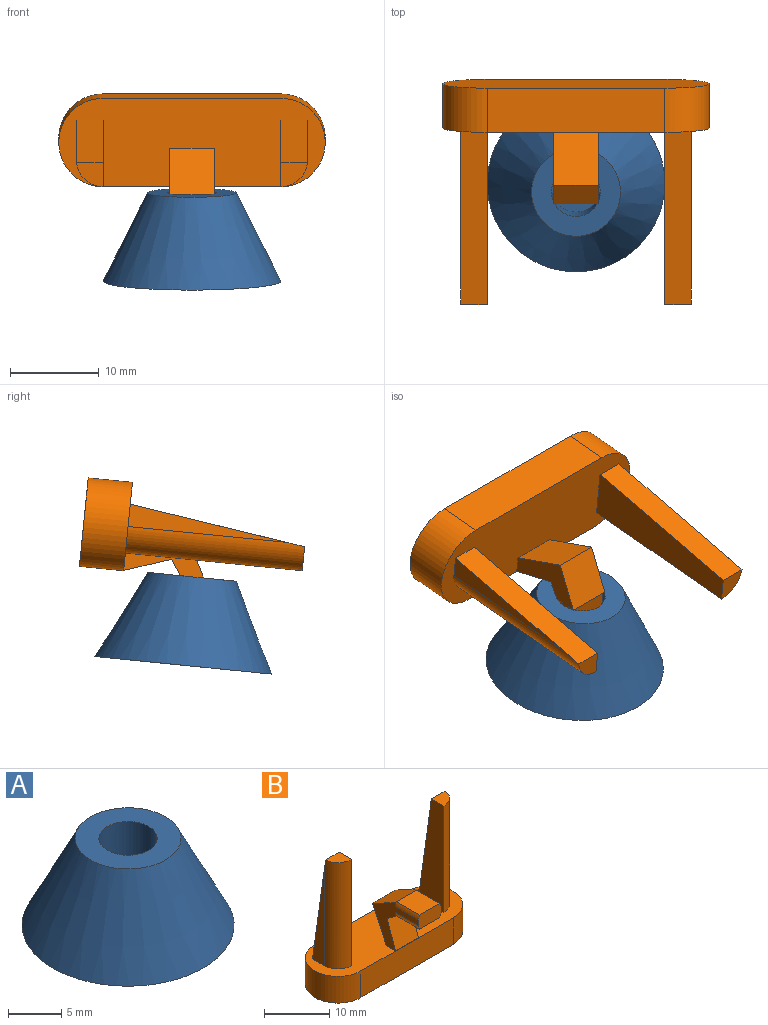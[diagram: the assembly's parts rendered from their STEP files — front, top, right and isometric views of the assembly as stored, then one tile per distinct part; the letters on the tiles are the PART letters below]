
ASSEMBLY  parts=2 mates=1
PART A: 5 faces, bbox 20x20x10 mm
  f0: plane 10x10mm, normal (0,0,1), area 54.8mm2, adj f2,f3
  f1: plane 20x20mm, normal (0,0,-1), area 314.2mm2, adj f2
  f2: cone r=5mm half-angle=26.6deg, axis (0,0,-1), area 526.9mm2, adj f0,f1
  f3: cylinder r=2.75mm len=5.5mm, axis (0,0,1), area 86.4mm2, adj f0,f4
  f4: plane 5.5x5.5mm, normal (0,0,1), area 23.8mm2, adj f3
PART B: 33 faces, bbox 30x14.9x25 mm
  f0: plane 0.82x0.32mm, normal (0,-1,0), area 0.1mm2, adj f22,f25,f31
  f1: plane 0.82x0.32mm, normal (0,-1,0), area 0.1mm2, adj f20,f25,f30
  f2: plane 0.82x0.32mm, normal (0,-1,0), area 0.1mm2, adj f20,f24,f28
  f3: plane 30x10mm, normal (0,0,1), area 239.4mm2, adj f4,f5,f6,f7,f9,f10,f11,f12
  f4: plane 20x5mm, normal (0,1,0), area 100mm2, adj f3,f5,f7,f8
  f5: cylinder r=5mm len=10mm, axis (0,0,-1), area 78.5mm2, adj f3,f4,f6,f8
  f6: plane 20x5mm, normal (0,-1,0), area 100mm2, adj f3,f5,f7,f8
  f7: cylinder r=5mm len=10mm, axis (0,0,-1), area 78.5mm2, adj f3,f4,f6,f8
  f8: plane 30x10mm, normal (0,0,-1), area 278.5mm2, adj f4,f5,f6,f7
  f9: plane 17.95x2.52mm, normal (-1,0,0), area 22.7mm2, adj f3,f10,f12
  f10: cylinder r=3mm len=20mm, axis (0,0,-1), area 94mm2, adj f3,f9,f11,f12,f13
  f11: plane 20x5.52mm, normal (1,0,0), area 82.4mm2, adj f3,f10,f12,f13
  f12: plane 20x3mm, normal (0,0.99,0.14), area 60.6mm2, adj f3,f9,f10,f11,f13
  f13: plane 2.99x2.71mm, normal (0,0,1), area 6.2mm2, adj f10,f11,f12
  f14: plane 20x3mm, normal (0,0.99,0.14), area 60.6mm2, adj f3,f15,f16,f17,f18
  f15: plane 20x5.52mm, normal (-1,0,0), area 82.4mm2, adj f3,f14,f16,f18
  f16: cylinder r=3mm len=20mm, axis (0,0,-1), area 94mm2, adj f3,f14,f15,f17,f18
  f17: plane 17.95x2.52mm, normal (1,0,0), area 22.7mm2, adj f3,f14,f16
  f18: plane 2.99x2.71mm, normal (0,0,1), area 6.2mm2, adj f14,f15,f16
  f19: plane 6.46x5mm, normal (0,0.91,-0.42), area 35.6mm2, adj f3,f20,f24,f25
  f20: plane 5x4.92mm, normal (0,0.47,0.88), area 27.8mm2, adj f1,f2,f19,f24,f25,f29
  f21: plane 0.82x0.32mm, normal (0,-1,0), area 0.1mm2, adj f22,f24,f27
  f22: plane 5x1.74mm, normal (0,-0.56,-0.83), area 10.5mm2, adj f0,f21,f23,f24,f25,f26
  f23: plane 5.24x5mm, normal (0,-0.95,0.32), area 27.7mm2, adj f3,f22,f24,f25
  f24: plane 9.92x9.06mm, normal (1,0,0), area 28.1mm2, adj f2,f3,f19,f20,f21,f22,f23,f27
  f25: plane 9.92x9.06mm, normal (-1,0,0), area 28.1mm2, adj f0,f1,f3,f19,f20,f22,f23,f30
  f26: plane 5x4.35mm, normal (0,0,-1), area 21.8mm2, adj f22,f27,f31,f32
  f27: cylinder r=2.55mm len=5mm, axis (0,1,0), area 4.5mm2, adj f21,f24,f26,f32
  f28: cylinder r=2.55mm len=5mm, axis (0,1,0), area 4.5mm2, adj f2,f24,f29,f32
  f29: plane 5x4.35mm, normal (0,0,1), area 21.8mm2, adj f20,f28,f30,f32
  f30: cylinder r=2.55mm len=5mm, axis (0,1,0), area 4.5mm2, adj f1,f25,f29,f32
  f31: cylinder r=2.55mm len=5mm, axis (0,1,0), area 4.5mm2, adj f0,f25,f26,f32
  f32: plane 5x2.65mm, normal (0,-1,0), area 12.8mm2, adj f24,f25,f26,f27,f28,f29,f30,f31
PLACE A rot(axis=(1,0,0),5.7deg) t=(-12.33,-27.1,19.12)mm
PLACE B rot(axis=(1,0,0),95.7deg) t=(-12.33,-15.91,35.23)mm
MATE fastened B.f27 <-> A.f3  axis (0,0.1,-1) through (-12.33,-27.6,24.09)mm
